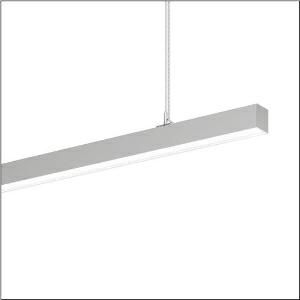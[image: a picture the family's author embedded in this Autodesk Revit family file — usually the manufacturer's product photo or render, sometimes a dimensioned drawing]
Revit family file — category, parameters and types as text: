
# Revit family: silica_21_51mx33tat7s
name_source: partatom
category: Lighting Fixtures
units: mm (PartAtom-declared; Revit-internal decimal feet)

## family parameters
Cut with Voids When Loaded = No
Host = Face
Light Source = No
Part Type = Normal
Room Calculation Point = No
Round Connector Dimension = Use Diameter
Shared = No

## types (1)
- --- (1 x LED, 5740 lm, 53.8 W, 6500K)
    Apparent Load = 54 VA
    CIE Flux Codes = 78 96 99 56 100
    Color Rendering = 80
    Color Temperature = 6500K
    Default Elevation = 1800 mm
    Description = Silica 21, office luminaire, primary optical cover: prismatic diffuser, of PMMA, CAT 2 (L<= 3000cd/m²), light emission: direct/indirect distribution, primary light characteristic: symmetric, installation type: suspended mounting, LED, rated luminous flux: 5.740lm, luminous efficacy: 102lm/W, light colour: 8tw, colour temperature: 2700..6500K, control gear: DALI DT8, with terminal, 3+2-pole, max. 2.5mm², mains connection: 220..240V, AC, 50/60Hz, rated input power: 56.5W, luminaire housing, of aluminium, metallic grey (RAL 9006), length: 1.204mm, width: 53mm, height: 53mm, protection rating (complete): IP20, insulation class (complete): insulation class I (protective earthing), certification: CE, permissible operating ambient temperature: 0..+35°C, standard: EN 50419, packaging unit: 1 piece
    Height = 53 mm
    Lamp = 1 x LED
    Lamp Light Flux = 5740 lm
    Lamp Power = 53.8 W
    Lamp count = 1
    Length = 1204 mm
    Luminous efficacy = 107 lm/W
    Manufacturer = Siteco
    ModVariant = No
    Model = 51MX33TAT7S
    Mounting Place = Ceiling
    Mounting Type = Pendant
    Number of Poles = 1
    OnlyDefault = Yes
    Power Factor = 1
    Product Name = Silica 21
    Product group = office luminaire | ceiling pendant
    ProductGroupID = 903
    Protection Class = Protection class I
    Protection Degree = IP 20
    RLX_Detail_Level = 1
    RLX_Emergency_Light_Flux = 0 lm
    RLX_Emergency_Type = 0
    RLX_Emergency_Type_DB = No
    RlxData = <blob elided: 20189 chars, md5=406b0a7b>
    Socket = socket
    Standby Power = 0 W
    System Light Flux = 5740 lm
    System Power = 54 W
    Type Comments = individual setting
    Type Image = l_1335864.jpg
    URL = http://relux.com
    VarID = @adj_140797
    Voltage = 0 V
    Weight = 0.00 kg
    Width = 53 mm

## geometry (parser evidence)
native form markers: Blend x4, Sweep x13
no freeform markers — native parametric forms only
